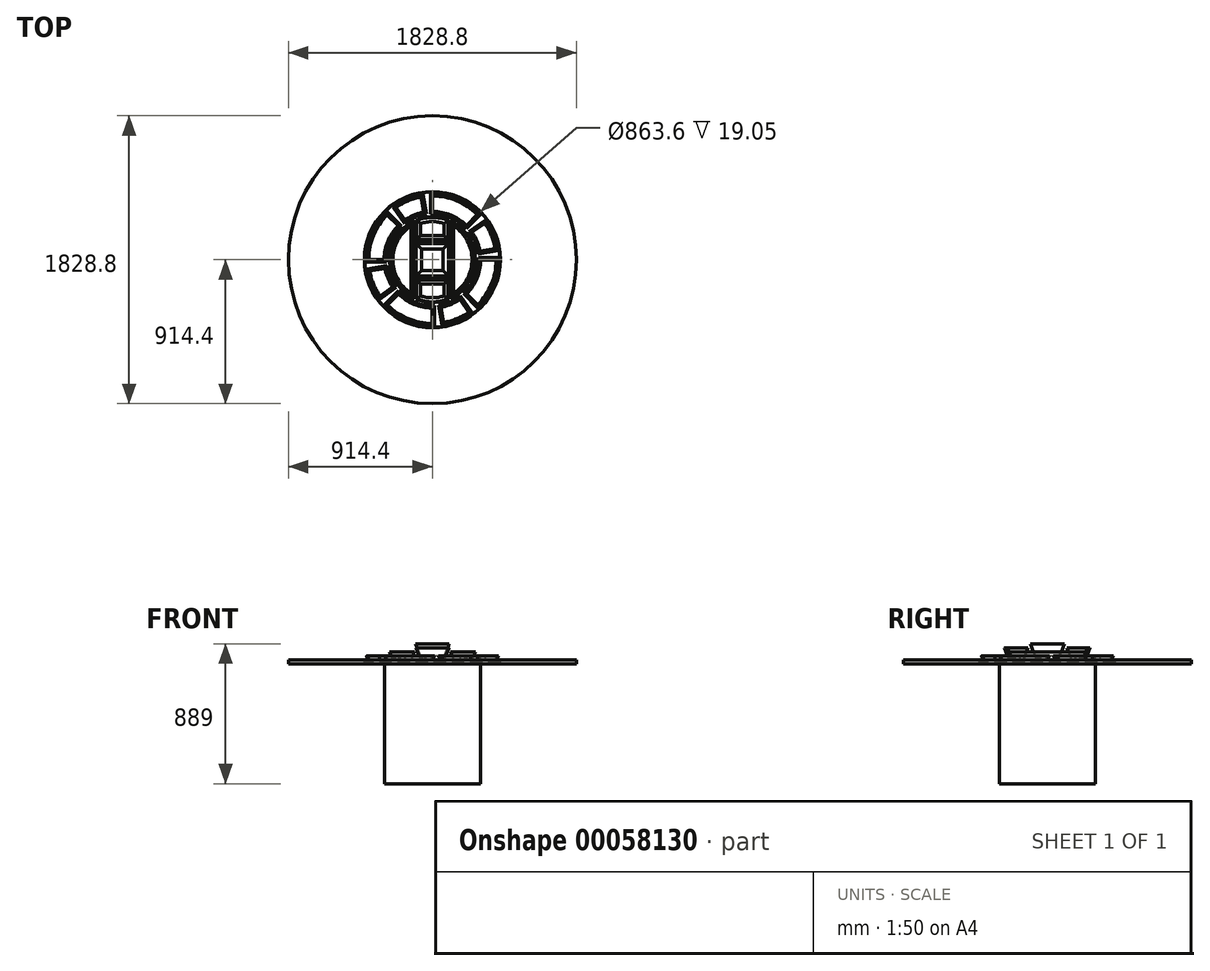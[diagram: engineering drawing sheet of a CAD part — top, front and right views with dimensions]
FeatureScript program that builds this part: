
annotation { "Feature Type Name" : "Feature", "Feature Type Description" : "" }
export const myFeature = defineFeature(function(context is Context, id is Id, definition is map)
    precondition{}
    {
        {
            var Q0;
            Q0=qCreatedBy(makeId("Top.planeOp"),FACE);
            var sketch = newSketch(context, id + "F0", { "sketchPlane" : qUnion([Q0])});
            skCircle(sketch, "E0", {"center": v(0, 0) * mm, "radius": 914.4 * mm});
            skSolve(sketch);
        }
        {
            var Q0;
            Q0=qSketchRegion(id+"F0",true);
            extrude(context, id + "F1", {"entities" : qUnion([Q0]), "depth" : 25.4 * mm});
        }
        {
            var Q0;
            Q0=makeQuery(id+"F1.opExtrude","CAP_FACE",FACE,{"disambiguationData":[OSD([sQuery(id+"F0.wireOp",EDGE,"E0")])],"isStart":false});
            var sketch = newSketch(context, id + "F2", { "sketchPlane" : qUnion([Q0])});
            skCircle(sketch, "E1", {"center": v(0, 0) * mm, "radius": 431.8 * mm});
            skSolve(sketch);
        }
        {
            var Q0;
            Q0=qSketchRegion(id+"F2",true);
            extrude(context, id + "F3", {"entities" : qUnion([Q0]), "operationType" : NewBodyOperationType.REMOVE, "oppositeDirection" : true, "depth" : 19.05 * mm});
        }
        {
            var Q0;
            Q0=makeQuery(id+"F3.boolean.opBoolean","COPY",FACE,{"derivedFrom":makeQuery(id+"F3.opExtrude","CAP_FACE",FACE,{"disambiguationData":[OSD([sQuery(id+"F2.wireOp",EDGE,"E1")])],"isStart":false})});
            var sketch = newSketch(context, id + "F4", { "sketchPlane" : qUnion([Q0])});
            skCircle(sketch, "E2", {"center": v(0, 0) * mm, "radius": 428.63 * mm});
            skSolve(sketch);
        }
        {
            var Q0;
            Q0=qSketchRegion(id+"F4",true);
            extrude(context, id + "F5", {"entities" : qUnion([Q0]), "depth" : 19.05 * mm});
        }
        {
            var Q0;
            Q0=makeQuery(id+"F1.opExtrude","CAP_FACE",FACE,{"disambiguationData":[OSD([sQuery(id+"F0.wireOp",EDGE,"E0")])],"isStart":true});
            var sketch = newSketch(context, id + "F6", { "sketchPlane" : qUnion([Q0])});
            skCircle(sketch, "E3", {"center": v(0, 0) * mm, "radius": 304.8 * mm});
            skSolve(sketch);
        }
        {
            var Q0;
            Q0=qSketchRegion(id+"F6",true);
            extrude(context, id + "F7", {"entities" : qUnion([Q0]), "operationType" : NewBodyOperationType.ADD, "depth" : 762 * mm});
        }
        {
            var Q0;
            Q0=makeQuery(id+"F5.opExtrude","CAP_FACE",FACE,{"disambiguationData":[OSD([sQuery(id+"F4.wireOp",EDGE,"E2")])],"isStart":false});
            var sketch = newSketch(context, id + "F8", { "sketchPlane" : qUnion([Q0])});
            skArc(sketch, "E4", {"start": v(-406.4, 0) * mm, "mid": v(-375.46, 155.52) * mm, "end": v(-287.37, 287.37) * mm});
            skArc(sketch, "E5", {"start": v(-304.8, 0) * mm, "mid": v(-281.6, 116.64) * mm, "end": v(-215.53, 215.53) * mm});
            skLineSegment(sketch, "E6", {"start": v(-406.4, 0) * mm, "end": v(-304.8, 0) * mm});
            skLineSegment(sketch, "E7", {"start": v(-287.37, 287.37) * mm, "end": v(-215.53, 215.53) * mm});
            skArc(sketch, "E8.1.0", {"start": v(0, -406.4) * mm, "mid": v(-155.52, -375.46) * mm, "end": v(-287.37, -287.37) * mm});
            skArc(sketch, "E8.1.1", {"start": v(0, -304.8) * mm, "mid": v(-116.64, -281.6) * mm, "end": v(-215.53, -215.53) * mm});
            skLineSegment(sketch, "E8.1.2", {"start": v(0, -406.4) * mm, "end": v(0, -304.8) * mm});
            skLineSegment(sketch, "E8.1.3", {"start": v(-287.37, -287.37) * mm, "end": v(-215.53, -215.53) * mm});
            skArc(sketch, "E8.2.0", {"start": v(406.4, 0) * mm, "mid": v(375.46, -155.52) * mm, "end": v(287.37, -287.37) * mm});
            skArc(sketch, "E8.2.1", {"start": v(304.8, 0) * mm, "mid": v(281.6, -116.64) * mm, "end": v(215.53, -215.53) * mm});
            skLineSegment(sketch, "E8.2.2", {"start": v(406.4, 0) * mm, "end": v(304.8, 0) * mm});
            skLineSegment(sketch, "E8.2.3", {"start": v(287.37, -287.37) * mm, "end": v(215.53, -215.53) * mm});
            skArc(sketch, "E9.2.3.0", {"start": v(0, 406.4) * mm, "mid": v(155.52, 375.46) * mm, "end": v(287.37, 287.37) * mm});
            skArc(sketch, "E9.4.3.0", {"start": v(0, 304.8) * mm, "mid": v(116.64, 281.6) * mm, "end": v(215.53, 215.53) * mm});
            skLineSegment(sketch, "E9.8.3.0", {"start": v(0, 406.4) * mm, "end": v(0, 304.8) * mm});
            skLineSegment(sketch, "E9.11.3.0", {"start": v(287.37, 287.37) * mm, "end": v(215.53, 215.53) * mm});
            skArc(sketch, "E10", {"start": v(-233.1, 332.9) * mm, "mid": v(-155.52, 375.46) * mm, "end": v(-70.57, 400.23) * mm});
            skArc(sketch, "E11", {"start": v(-174.83, 249.68) * mm, "mid": v(-116.64, 281.6) * mm, "end": v(-52.93, 300.17) * mm});
            skLineSegment(sketch, "E12", {"start": v(-233.1, 332.9) * mm, "end": v(-174.83, 249.68) * mm});
            skLineSegment(sketch, "E13", {"start": v(-70.57, 400.23) * mm, "end": v(-52.93, 300.17) * mm});
            skLineSegment(sketch, "E14.1.0", {"start": v(-332.9, -233.1) * mm, "end": v(-249.68, -174.83) * mm});
            skLineSegment(sketch, "E14.1.1", {"start": v(-400.23, -70.57) * mm, "end": v(-300.17, -52.93) * mm});
            skArc(sketch, "E14.1.2", {"start": v(-249.68, -174.83) * mm, "mid": v(-281.6, -116.64) * mm, "end": v(-300.17, -52.93) * mm});
            skArc(sketch, "E14.1.3", {"start": v(-332.9, -233.1) * mm, "mid": v(-375.46, -155.52) * mm, "end": v(-400.23, -70.57) * mm});
            skLineSegment(sketch, "E14.2.0", {"start": v(233.1, -332.9) * mm, "end": v(174.83, -249.68) * mm});
            skLineSegment(sketch, "E14.2.1", {"start": v(70.57, -400.23) * mm, "end": v(52.93, -300.17) * mm});
            skArc(sketch, "E14.2.2", {"start": v(174.83, -249.68) * mm, "mid": v(116.64, -281.6) * mm, "end": v(52.93, -300.17) * mm});
            skArc(sketch, "E14.2.3", {"start": v(233.1, -332.9) * mm, "mid": v(155.52, -375.46) * mm, "end": v(70.57, -400.23) * mm});
            skLineSegment(sketch, "E14.3.0", {"start": v(332.9, 233.1) * mm, "end": v(249.68, 174.83) * mm});
            skLineSegment(sketch, "E14.3.1", {"start": v(400.23, 70.57) * mm, "end": v(300.17, 52.93) * mm});
            skArc(sketch, "E14.3.2", {"start": v(249.68, 174.83) * mm, "mid": v(281.6, 116.64) * mm, "end": v(300.17, 52.93) * mm});
            skArc(sketch, "E14.3.3", {"start": v(332.9, 233.1) * mm, "mid": v(375.46, 155.52) * mm, "end": v(400.23, 70.57) * mm});
            skSolve(sketch);
        }
        {
            var Q0;
            Q0 = qSketchRegion(id + "F8", true);
            extrude(context, id + "F9", {"entities" : qUnion([Q0]), "depth" : 22.86 * mm, "hasDraft" : true, "draftAngle" : 30 * degree});
        }
        {
            var Q0;
            Q0=makeQuery(id+"F9.opExtrude","CAP_FACE",FACE,{"disambiguationData":[OSD([sQuery(id+"F8.wireOp",EDGE,"E4"),sQuery(id+"F8.wireOp",EDGE,"E5"),sQuery(id+"F8.wireOp",EDGE,"E6"),sQuery(id+"F8.wireOp",EDGE,"E7")])],"isStart":false});
            var Q1;
            Q1=makeQuery(id+"F9.opExtrude","CAP_FACE",FACE,{"disambiguationData":[OSD([sQuery(id+"F8.wireOp",EDGE,"E10"),sQuery(id+"F8.wireOp",EDGE,"E11"),sQuery(id+"F8.wireOp",EDGE,"E12"),sQuery(id+"F8.wireOp",EDGE,"E13")])],"isStart":false});
            var Q2;
            Q2=makeQuery(id+"F9.opExtrude","CAP_FACE",FACE,{"disambiguationData":[OSD([sQuery(id+"F8.wireOp",EDGE,"E9.2.3.0"),sQuery(id+"F8.wireOp",EDGE,"E9.4.3.0"),sQuery(id+"F8.wireOp",EDGE,"E9.8.3.0"),sQuery(id+"F8.wireOp",EDGE,"E9.11.3.0")])],"isStart":false});
            var Q3;
            Q3=makeQuery(id+"F9.opExtrude","CAP_FACE",FACE,{"disambiguationData":[OSD([sQuery(id+"F8.wireOp",EDGE,"E14.3.0"),sQuery(id+"F8.wireOp",EDGE,"E14.3.1"),sQuery(id+"F8.wireOp",EDGE,"E14.3.2"),sQuery(id+"F8.wireOp",EDGE,"E14.3.3")])],"isStart":false});
            var Q4;
            Q4=makeQuery(id+"F9.opExtrude","CAP_FACE",FACE,{"disambiguationData":[OSD([sQuery(id+"F8.wireOp",EDGE,"E8.2.0"),sQuery(id+"F8.wireOp",EDGE,"E8.2.1"),sQuery(id+"F8.wireOp",EDGE,"E8.2.2"),sQuery(id+"F8.wireOp",EDGE,"E8.2.3")])],"isStart":false});
            var Q5;
            Q5=makeQuery(id+"F9.opExtrude","CAP_FACE",FACE,{"disambiguationData":[OSD([sQuery(id+"F8.wireOp",EDGE,"E14.2.0"),sQuery(id+"F8.wireOp",EDGE,"E14.2.1"),sQuery(id+"F8.wireOp",EDGE,"E14.2.2"),sQuery(id+"F8.wireOp",EDGE,"E14.2.3")])],"isStart":false});
            var Q6;
            Q6=makeQuery(id+"F9.opExtrude","CAP_FACE",FACE,{"disambiguationData":[OSD([sQuery(id+"F8.wireOp",EDGE,"E8.1.0"),sQuery(id+"F8.wireOp",EDGE,"E8.1.1"),sQuery(id+"F8.wireOp",EDGE,"E8.1.2"),sQuery(id+"F8.wireOp",EDGE,"E8.1.3")])],"isStart":false});
            var Q7;
            Q7=makeQuery(id+"F9.opExtrude","CAP_FACE",FACE,{"disambiguationData":[OSD([sQuery(id+"F8.wireOp",EDGE,"E14.1.0"),sQuery(id+"F8.wireOp",EDGE,"E14.1.1"),sQuery(id+"F8.wireOp",EDGE,"E14.1.2"),sQuery(id+"F8.wireOp",EDGE,"E14.1.3")])],"isStart":false});
            shell(context, id + "F10", {"entities" : qUnion([Q0, Q1, Q2, Q3, Q4, Q5, Q6, Q7]), "thickness" : 3.17 * mm});
        }
        {
            var Q0;
            Q0=makeQuery(id+"F5.opExtrude","CAP_FACE",FACE,{"disambiguationData":[OSD([sQuery(id+"F4.wireOp",EDGE,"E2")])],"isStart":false});
            var sketch = newSketch(context, id + "F11", { "sketchPlane" : qUnion([Q0])});
            skArc(sketch, "E15", {"start": v(133.35, 216.18) * mm, "mid": v(254, 0) * mm, "end": v(133.35, -216.18) * mm});
            skLineSegment(sketch, "E16", {"start": v(133.35, 0) * mm, "end": v(133.35, -216.18) * mm});
            skLineSegment(sketch, "E17", {"start": v(133.35, 0) * mm, "end": v(133.35, 216.18) * mm});
            skLineSegment(sketch, "E18.1.0", {"start": v(-133.35, 0) * mm, "end": v(-133.35, -216.18) * mm});
            skLineSegment(sketch, "E18.1.1", {"start": v(-133.35, 0) * mm, "end": v(-133.35, 216.18) * mm});
            skArc(sketch, "E18.1.2", {"start": v(-133.35, -216.18) * mm, "mid": v(-254, 0) * mm, "end": v(-133.35, 216.18) * mm});
            skSolve(sketch);
        }
        {
            var Q0;
            Q0 = qSketchRegion(id + "F11", true);
            extrude(context, id + "F12", {"entities" : qUnion([Q0]), "depth" : 50.8 * mm, "hasDraft" : true, "draftAngle" : 20 * degree});
        }
        {
            var Q0;
            Q0=makeQuery(id+"F12.opExtrude","CAP_FACE",FACE,{"disambiguationData":[OSD([sQuery(id+"F11.wireOp",EDGE,"E18.1.0"),sQuery(id+"F11.wireOp",EDGE,"E18.1.1"),sQuery(id+"F11.wireOp",EDGE,"E18.1.2")])],"isStart":false});
            var Q1;
            Q1=makeQuery(id+"F12.opExtrude","CAP_FACE",FACE,{"disambiguationData":[OSD([sQuery(id+"F11.wireOp",EDGE,"E15"),sQuery(id+"F11.wireOp",EDGE,"E16"),sQuery(id+"F11.wireOp",EDGE,"E17")])],"isStart":false});
            shell(context, id + "F13", {"entities" : qUnion([Q0, Q1]), "thickness" : 3.17 * mm});
        }
        {
            var Q0;
            Q0=makeQuery(id+"F5.opExtrude","CAP_FACE",FACE,{"disambiguationData":[OSD([sQuery(id+"F4.wireOp",EDGE,"E2")])],"isStart":false});
            var sketch = newSketch(context, id + "F14", { "sketchPlane" : qUnion([Q0])});
            skArc(sketch, "E19", {"start": v(76.2, -231.63) * mm, "mid": v(0, -243.84) * mm, "end": v(-76.2, -231.63) * mm});
            skLineSegment(sketch, "E20", {"start": v(76.2, -231.63) * mm, "end": v(76.2, -152.4) * mm});
            skLineSegment(sketch, "E21", {"start": v(76.2, -152.4) * mm, "end": v(-76.2, -152.4) * mm});
            skLineSegment(sketch, "E22", {"start": v(-76.2, -152.4) * mm, "end": v(-76.2, -231.63) * mm});
            skArc(sketch, "E23.1.0", {"start": v(-76.2, 231.63) * mm, "mid": v(0, 243.84) * mm, "end": v(76.2, 231.63) * mm});
            skLineSegment(sketch, "E23.1.1", {"start": v(-76.2, 231.63) * mm, "end": v(-76.2, 152.4) * mm});
            skLineSegment(sketch, "E23.1.2", {"start": v(-76.2, 152.4) * mm, "end": v(76.2, 152.4) * mm});
            skLineSegment(sketch, "E23.1.3", {"start": v(76.2, 152.4) * mm, "end": v(76.2, 231.63) * mm});
            skSolve(sketch);
        }
        {
            var Q0;
            Q0 = qSketchRegion(id + "F14", true);
            extrude(context, id + "F15", {"entities" : qUnion([Q0]), "depth" : 76.2 * mm, "hasDraft" : true, "draftAngle" : 20 * degree});
        }
        {
            var Q0;
            Q0=makeQuery(id+"F15.opExtrude","CAP_FACE",FACE,{"disambiguationData":[OSD([sQuery(id+"F14.wireOp",EDGE,"E23.1.0"),sQuery(id+"F14.wireOp",EDGE,"E23.1.1"),sQuery(id+"F14.wireOp",EDGE,"E23.1.2"),sQuery(id+"F14.wireOp",EDGE,"E23.1.3")])],"isStart":false});
            var Q1;
            Q1=makeQuery(id+"F15.opExtrude","CAP_FACE",FACE,{"disambiguationData":[OSD([sQuery(id+"F14.wireOp",EDGE,"a6812c06-e5b6-4f76-84a8-4b2d7a4645f0.rect.bottom"),sQuery(id+"F14.wireOp",EDGE,"a6812c06-e5b6-4f76-84a8-4b2d7a4645f0.rect.top"),sQuery(id+"F14.wireOp",EDGE,"a6812c06-e5b6-4f76-84a8-4b2d7a4645f0.rect.left"),sQuery(id+"F14.wireOp",EDGE,"a6812c06-e5b6-4f76-84a8-4b2d7a4645f0.rect.right")])],"isStart":false});
            var Q2;
            Q2=makeQuery(id+"F15.opExtrude","CAP_FACE",FACE,{"disambiguationData":[OSD([sQuery(id+"F14.wireOp",EDGE,"E19"),sQuery(id+"F14.wireOp",EDGE,"E20"),sQuery(id+"F14.wireOp",EDGE,"E21"),sQuery(id+"F14.wireOp",EDGE,"E22")])],"isStart":false});
            shell(context, id + "F16", {"entities" : qUnion([Q0, Q1, Q2]), "thickness" : 3.17 * mm});
        }
        {
            var Q0;
            Q0=makeQuery(id+"F5.opExtrude","CAP_FACE",FACE,{"disambiguationData":[OSD([sQuery(id+"F4.wireOp",EDGE,"E2")])],"isStart":false});
            var sketch = newSketch(context, id + "F17", { "sketchPlane" : qUnion([Q0])});
            skPoint(sketch, "E24.center", {"position": v(0, 0) * mm});
            skLineSegment(sketch, "E25.rect.bottom", {"start": v(69.85, -69.85) * mm, "end": v(-69.85, -69.85) * mm});
            skLineSegment(sketch, "E25.rect.top", {"start": v(69.85, 69.85) * mm, "end": v(-69.85, 69.85) * mm});
            skLineSegment(sketch, "E25.rect.left", {"start": v(69.85, -69.85) * mm, "end": v(69.85, 69.85) * mm});
            skLineSegment(sketch, "E25.rect.right", {"start": v(-69.85, -69.85) * mm, "end": v(-69.85, 69.85) * mm});
            skSolve(sketch);
        }
        {
            var Q0;
            Q0 = qSketchRegion(id + "F17", true);
            extrude(context, id + "F18", {"entities" : qUnion([Q0]), "depth" : 101.6 * mm, "hasDraft" : true, "draftAngle" : 20 * degree});
        }
        {
            var Q0;
            Q0=makeQuery(id+"F18.opExtrude","CAP_FACE",FACE,{"disambiguationData":[OSD([sQuery(id+"F17.wireOp",EDGE,"E25.rect.bottom"),sQuery(id+"F17.wireOp",EDGE,"E25.rect.top"),sQuery(id+"F17.wireOp",EDGE,"E25.rect.left"),sQuery(id+"F17.wireOp",EDGE,"E25.rect.right")])],"isStart":false});
            shell(context, id + "F19", {"entities" : qUnion([Q0]), "thickness" : 3.17 * mm});
        }
    });
